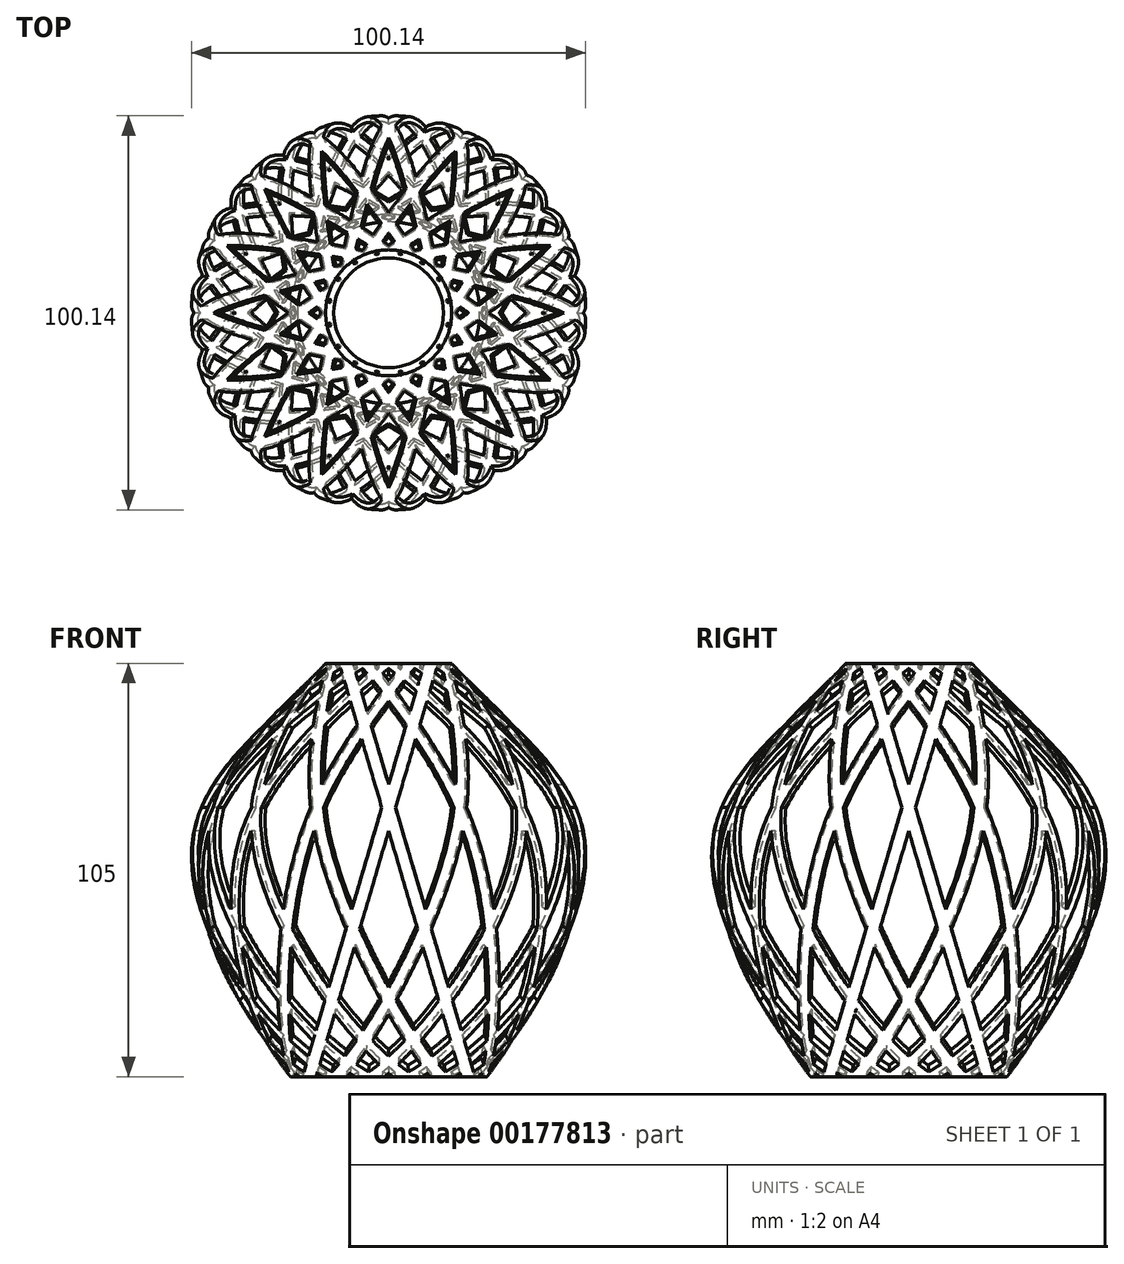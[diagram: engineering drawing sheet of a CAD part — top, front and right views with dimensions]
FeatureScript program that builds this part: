
annotation { "Feature Type Name" : "Feature", "Feature Type Description" : "" }
export const myFeature = defineFeature(function(context is Context, id is Id, definition is map)
    precondition{}
    {
        {
            var Q0;
            Q0=qCreatedBy(makeId("Front.planeOp"),FACE);
            var sketch = newSketch(context, id + "F0", { "sketchPlane" : qUnion([Q0])});
            skFitSpline(sketch, "E0", {"points": [v(-25, -53.33) * mm, v(-49.3, 9.72) * mm, v(-16, 51.67) * mm], "startDerivative": vector(-90.96, 121.73) * mm, "endDerivative": vector(81.84, 87.2) * mm});
            skLineSegment(sketch, "E1", {"start": v(-16, 51.67) * mm, "end": v(0, 51.67) * mm});
            skLineSegment(sketch, "E2", {"start": v(-25, -53.33) * mm, "end": v(0, -53.33) * mm});
            skLineSegment(sketch, "E3", {"start": v(0, -53.33) * mm, "end": v(0, 51.67) * mm});
            skSolve(sketch);
        }
        {
            var Q0;
            Q0=makeQuery(id+"F0.imprint","IMPRINT",FACE,{"disambiguationData":[TD([[makeQuery(id+"F0.imprint","IMPRINT",EDGE,{"derivedFrom":sQuery(id+"F0.wireOp",EDGE,"E0")}),-1.0]])]});
            var Q1;
            Q1=sQuery(id+"F0.wireOp",EDGE,"E3");
            revolve(context, id + "F1", {"entities" : qUnion([Q0]), "axis" : qUnion([Q1]), "revolveType" : RevolveType.FULL});
        }
        {
            var Q0;
            Q0=makeQuery(id+"F1.opRevolve","SWEPT_FACE",FACE,{"disambiguationData":[OSD([sQuery(id+"F0.wireOp",EDGE,"E1")])]});
            var Q1;
            Q1=makeQuery(id+"F1.opRevolve","SWEPT_FACE",FACE,{"disambiguationData":[OSD([sQuery(id+"F0.wireOp",EDGE,"E2")])]});
            shell(context, id + "F2", {"entities" : qUnion([Q0, Q1]), "thickness" : 1.5 * mm});
        }
        {
            var Q0;
            Q0=qCreatedBy(makeId("Front.planeOp"),FACE);
            var sketch = newSketch(context, id + "F3", { "sketchPlane" : qUnion([Q0])});
            skFitSpline(sketch, "E4", {"points": [v(24.1, -54.55) * mm, v(24.4, -54.14) * mm, v(24.7, -53.74) * mm, v(25, -53.33) * mm, v(41.04, -31.87) * mm, v(64.47, 12.37) * mm, v(28.85, 37.98) * mm, v(16, 51.67) * mm, v(15.68, 52) * mm, v(15.36, 52.35) * mm, v(15.04, 52.7) * mm], "construction": true});
            skFitSpline(sketch, "E5", {"points": [v(-15.04, 52.7) * mm, v(-15.36, 52.35) * mm, v(-15.68, 52) * mm, v(-16, 51.67) * mm, v(-28.85, 37.98) * mm, v(-64.47, 12.37) * mm, v(-41.04, -31.87) * mm, v(-25, -53.33) * mm, v(-24.7, -53.74) * mm, v(-24.4, -54.14) * mm, v(-24.1, -54.55) * mm], "construction": true});
            skLineSegment(sketch, "E6", {"start": v(12.8, 52.48) * mm, "end": v(-18.56, -53.84) * mm});
            skLineSegment(sketch, "E7", {"start": v(9.3, 52.48) * mm, "end": v(-22.06, -53.84) * mm});
            skLineSegment(sketch, "E8", {"start": v(9.3, 52.48) * mm, "end": v(12.8, 52.48) * mm});
            skLineSegment(sketch, "E9", {"start": v(-22.06, -53.84) * mm, "end": v(-18.56, -53.84) * mm});
            skSolve(sketch);
        }
        {
            var Q0;
            Q0=makeQuery(id+"F3.imprint","IMPRINT",FACE,{"disambiguationData":[TD([[makeQuery(id+"F3.imprint","IMPRINT",EDGE,{"derivedFrom":sQuery(id+"F3.wireOp",EDGE,"E6")}),-1.0]])]});
            extrude(context, id + "F4", {"entities" : qUnion([Q0]), "endBound" : BoundingType.SYMMETRIC, "depth" : 120 * mm});
        }
        {
            var Q0;
            Q0=makeQuery(id+"F1.opRevolve","SWEPT_BODY",BODY,{"disambiguationData":[OSD([sQuery(id+"F0.wireOp",EDGE,"E0"),sQuery(id+"F0.wireOp",EDGE,"E1"),sQuery(id+"F0.wireOp",EDGE,"E2"),sQuery(id+"F0.wireOp",EDGE,"E3")])]});
            var Q1;
            Q1=makeQuery(id+"F4.opExtrude","SWEPT_BODY",BODY,{"disambiguationData":[OSD([sQuery(id+"F3.wireOp",EDGE,"E6"),sQuery(id+"F3.wireOp",EDGE,"E7"),sQuery(id+"F3.wireOp",EDGE,"E8"),sQuery(id+"F3.wireOp",EDGE,"E9")])]});
            booleanBodies(context, id + "F5", {"operationType" : BooleanOperationType.INTERSECTION, "tools" : qUnion([Q0, Q1])});
        }
        {
            var Q0;
            Q0=qCreatedBy(makeId("Front.planeOp"),FACE);
            var sketch = newSketch(context, id + "F6", { "sketchPlane" : qUnion([Q0])});
            skLineSegment(sketch, "E10", {"start": v(0, 70.28) * mm, "end": v(0, -67.37) * mm, "construction": true});
            skSolve(sketch);
        }
        {
            var Q0;
            Q0=makeQuery(id+"F5.opBoolean","INTERSECT",BODY,{"disambiguationData":[OD(0.0)],"derivedFrom":[makeQuery(id+"F1.opRevolve","SWEPT_BODY",BODY,{"disambiguationData":[OSD([sQuery(id+"F0.wireOp",EDGE,"E0"),sQuery(id+"F0.wireOp",EDGE,"E1"),sQuery(id+"F0.wireOp",EDGE,"E2"),sQuery(id+"F0.wireOp",EDGE,"E3")])]}),makeQuery(id+"F4.opExtrude","SWEPT_BODY",BODY,{"disambiguationData":[OSD([sQuery(id+"F3.wireOp",EDGE,"E6"),sQuery(id+"F3.wireOp",EDGE,"E7"),sQuery(id+"F3.wireOp",EDGE,"E8"),sQuery(id+"F3.wireOp",EDGE,"E9")])]})]});
            var Q1;
            Q1=sQuery(id+"F6.wireOp",EDGE,"E10");
            circularPattern(context, id + "F7", {"operationType" : NewBodyOperationType.ADD, "entities" : qUnion([Q0]), "axis" : qUnion([Q1]), "angle" : 360 * degree, "instanceCount" : 16, "oppositeDirection" : true, "equalSpace" : true});
        }
        {
            var Q0;
            Q0=makeQuery(id+"F5.opBoolean","INTERSECT",BODY,{"disambiguationData":[OD(1.0)],"derivedFrom":[makeQuery(id+"F1.opRevolve","SWEPT_BODY",BODY,{"disambiguationData":[OSD([sQuery(id+"F0.wireOp",EDGE,"E0"),sQuery(id+"F0.wireOp",EDGE,"E1"),sQuery(id+"F0.wireOp",EDGE,"E2"),sQuery(id+"F0.wireOp",EDGE,"E3")])]}),makeQuery(id+"F4.opExtrude","SWEPT_BODY",BODY,{"disambiguationData":[OSD([sQuery(id+"F3.wireOp",EDGE,"E6"),sQuery(id+"F3.wireOp",EDGE,"E7"),sQuery(id+"F3.wireOp",EDGE,"E8"),sQuery(id+"F3.wireOp",EDGE,"E9")])]})]});
            var Q1;
            Q1=sQuery(id+"F6.wireOp",EDGE,"E10");
            circularPattern(context, id + "F8", {"operationType" : NewBodyOperationType.ADD, "entities" : qUnion([Q0]), "axis" : qUnion([Q1]), "angle" : 360 * degree, "instanceCount" : 16, "equalSpace" : true});
        }
    });
